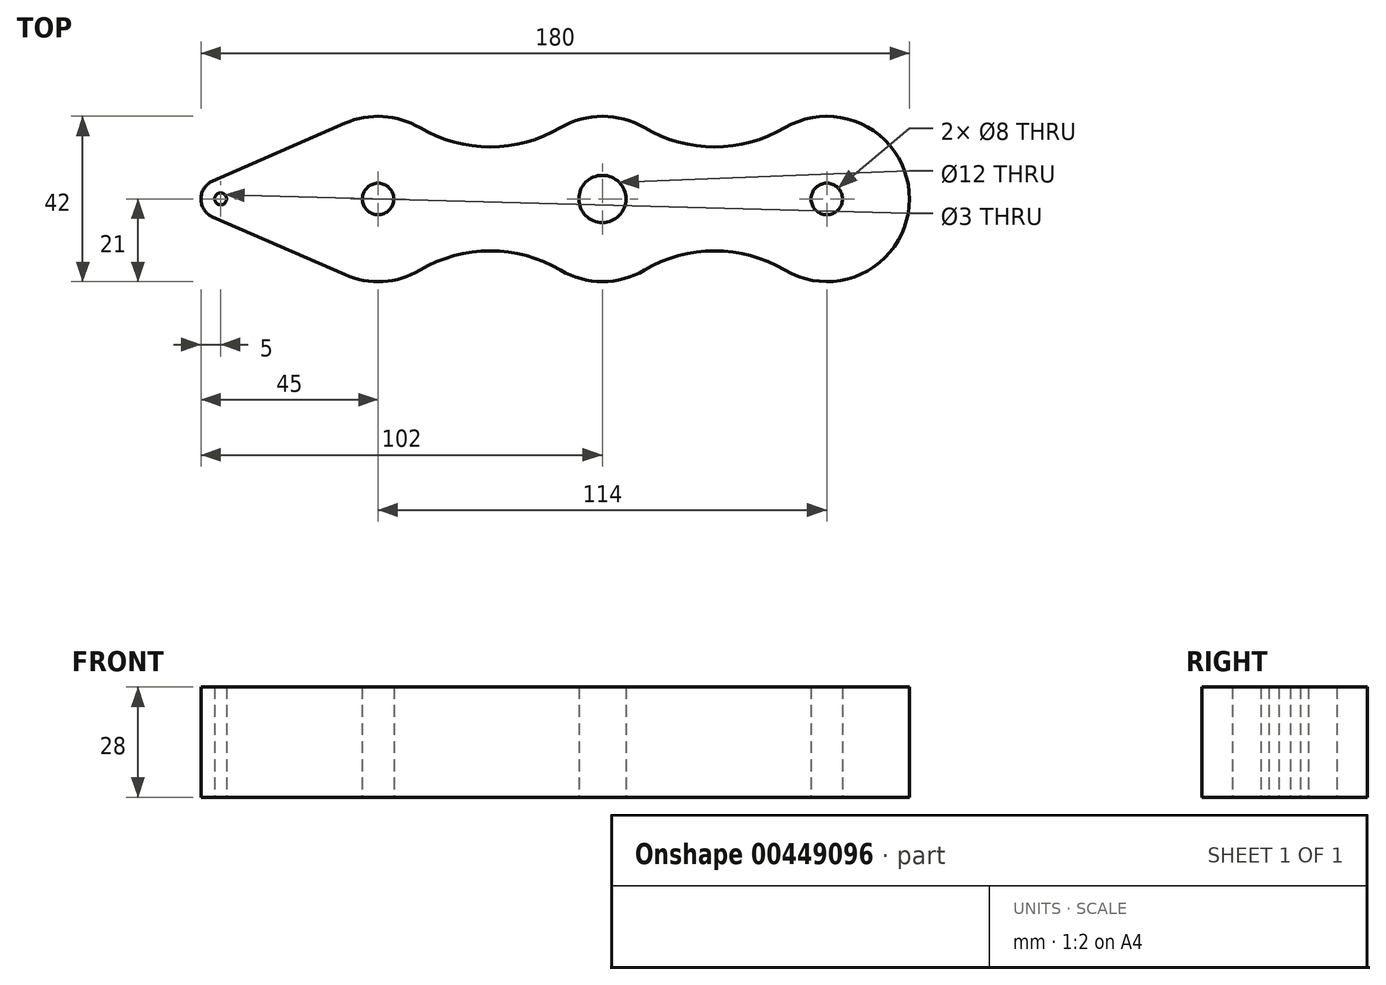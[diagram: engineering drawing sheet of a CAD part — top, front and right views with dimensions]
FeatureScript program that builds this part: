
annotation { "Feature Type Name" : "Feature", "Feature Type Description" : "" }
export const myFeature = defineFeature(function(context is Context, id is Id, definition is map)
    precondition{}
    {
        {
            var Q0;
            Q0=qCreatedBy(makeId("Top.planeOp"),FACE);
            var sketch = newSketch(context, id + "F0", { "sketchPlane" : qUnion([Q0])});
            skArc(sketch, "E0", {"start": v(-10.66, -18.1) * mm, "mid": v(21, 0) * mm, "end": v(-10.66, 18.1) * mm});
            skArc(sketch, "E1", {"start": v(-67.66, -18.1) * mm, "mid": v(-57, -21) * mm, "end": v(-46.34, -18.1) * mm});
            skArc(sketch, "E2", {"start": v(-122.4, -19.25) * mm, "mid": v(-112.73, -20.96) * mm, "end": v(-103.34, -18.1) * mm});
            skArc(sketch, "E3", {"start": v(-156, 4.58) * mm, "mid": v(-159, 0) * mm, "end": v(-156, -4.58) * mm});
            skLineSegment(sketch, "E4", {"start": v(-156, -4.58) * mm, "end": v(-122.4, -19.25) * mm});
            skLineSegment(sketch, "E5", {"start": v(-156, 4.58) * mm, "end": v(-122.4, 19.25) * mm});
            skCircle(sketch, "E6", {"center": v(-114, 0) * mm, "radius": 4 * mm});
            skCircle(sketch, "E7", {"center": v(-57, 0) * mm, "radius": 6 * mm});
            skCircle(sketch, "E8", {"center": v(0, 0) * mm, "radius": 4 * mm});
            skArc(sketch, "E9", {"start": v(-46.34, 18.1) * mm, "mid": v(-28.5, 13.22) * mm, "end": v(-10.66, 18.1) * mm});
            skArc(sketch, "E10.trimOffspring", {"start": v(-103.34, 18.1) * mm, "mid": v(-112.73, 20.96) * mm, "end": v(-122.4, 19.25) * mm});
            skPoint(sketch, "E11.start.orphan", {"position": v(-85.5, 0) * mm});
            skArc(sketch, "E12.1.0.0", {"start": v(-103.34, 18.1) * mm, "mid": v(-85.5, 13.22) * mm, "end": v(-67.66, 18.1) * mm});
            skArc(sketch, "E13.MirrorCS", {"start": v(-103.34, -18.1) * mm, "mid": v(-85.5, -13.22) * mm, "end": v(-67.66, -18.1) * mm});
            skArc(sketch, "E14.MirrorCS", {"start": v(-46.34, -18.1) * mm, "mid": v(-28.5, -13.22) * mm, "end": v(-10.66, -18.1) * mm});
            skArc(sketch, "E15.trimOffspring", {"start": v(-46.34, 18.1) * mm, "mid": v(-57, 21) * mm, "end": v(-67.66, 18.1) * mm});
            skCircle(sketch, "E16", {"center": v(-154, 0) * mm, "radius": 1.5 * mm});
            skSolve(sketch);
        }
        {
            var Q0;
            Q0=makeQuery(id+"F0.imprint","IMPRINT",FACE,{"disambiguationData":[TD([[makeQuery(id+"F0.imprint","IMPRINT",EDGE,{"derivedFrom":sQuery(id+"F0.wireOp",EDGE,"E0")}),1.0]])]});
            extrude(context, id + "F1", {"entities" : qUnion([Q0]), "depth" : 28 * mm});
        }
    });
